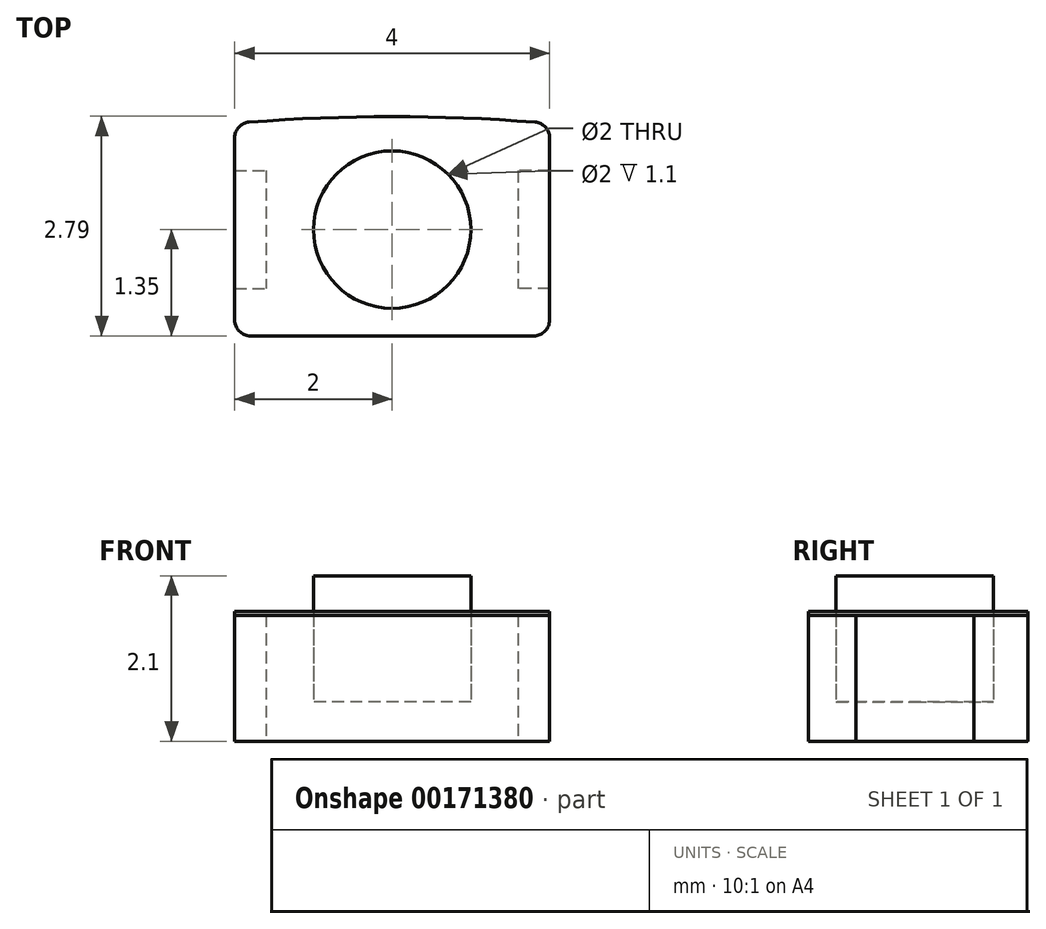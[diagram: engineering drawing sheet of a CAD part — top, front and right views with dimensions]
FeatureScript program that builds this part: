
annotation { "Feature Type Name" : "Feature", "Feature Type Description" : "" }
export const myFeature = defineFeature(function(context is Context, id is Id, definition is map)
    precondition{}
    {
        {
            var Q0;
            Q0=qCreatedBy(makeId("Top.planeOp"),FACE);
            var sketch = newSketch(context, id + "F0", { "sketchPlane" : qUnion([Q0])});
            skLineSegment(sketch, "E0.bottom", {"start": v(-2, 1.35) * mm, "end": v(2, 1.35) * mm});
            skLineSegment(sketch, "E0.top", {"start": v(-2, -1.35) * mm, "end": v(2, -1.35) * mm});
            skLineSegment(sketch, "E0.left", {"start": v(-2, 1.35) * mm, "end": v(-2, -1.35) * mm});
            skLineSegment(sketch, "E0.right", {"start": v(2, 1.35) * mm, "end": v(2, -1.35) * mm});
            skPoint(sketch, "E0.middle", {"position": v(0, 0) * mm});
            skLineSegment(sketch, "E1", {"start": v(0, 1.42) * mm, "end": v(0, -1.42) * mm});
            skPoint(sketch, "E1.endSnap0", {"position": v(0, -1.35) * mm});
            skArc(sketch, "E2", {"start": v(2, 1.35) * mm, "mid": v(0, 1.44) * mm, "end": v(-2, 1.35) * mm});
            skArc(sketch, "E3.MirrorCS", {"start": v(2, -1.35) * mm, "mid": v(0, -1.44) * mm, "end": v(-2, -1.35) * mm});
            skCircle(sketch, "E4", {"center": v(0, 0) * mm, "radius": 1 * mm});
            skLineSegment(sketch, "E5.bottom", {"start": v(-2, 0.75) * mm, "end": v(-1.6, 0.75) * mm});
            skLineSegment(sketch, "E5.top", {"start": v(-2, -0.75) * mm, "end": v(-1.6, -0.75) * mm});
            skLineSegment(sketch, "E5.left", {"start": v(-2, 0.75) * mm, "end": v(-2, -0.75) * mm});
            skLineSegment(sketch, "E5.right", {"start": v(-1.6, 0.75) * mm, "end": v(-1.6, -0.75) * mm});
            skPoint(sketch, "E6", {"position": v(-1.6, 0) * mm});
            skLineSegment(sketch, "E7.MirrorCS", {"start": v(2, -0.75) * mm, "end": v(1.6, -0.75) * mm});
            skLineSegment(sketch, "E8.MirrorCS", {"start": v(2, 0.75) * mm, "end": v(2, -0.75) * mm});
            skLineSegment(sketch, "E9.MirrorCS", {"start": v(2, 0.75) * mm, "end": v(1.6, 0.75) * mm});
            skLineSegment(sketch, "E10.MirrorCS", {"start": v(1.6, 0.75) * mm, "end": v(1.6, -0.75) * mm});
            skSolve(sketch);
        }
        {
            var Q0;
            {var subQ7=sQuery(id+"F0.wireOp",EDGE,"E5.bottom");Q0=makeQuery(id+"F0.imprint","IMPRINT",FACE,{"disambiguationData":[TD([[makeQuery(id+"F0.imprint","IMPRINT",EDGE,{"derivedFrom":subQ7}),1.0]])]});}
            var Q1;
            {var subQ0=sQuery(id+"F0.wireOp",EDGE,"E2");Q1=makeQuery(id+"F0.imprint","IMPRINT",FACE,{"disambiguationData":[TD([[makeQuery(id+"F0.imprint","IMPRINT",EDGE,{"derivedFrom":subQ0}),1.0]])]});}
            var Q2;
            {var subQ4=sQuery(id+"F0.wireOp",EDGE,"E7.MirrorCS");Q2=makeQuery(id+"F0.imprint","IMPRINT",FACE,{"disambiguationData":[TD([[makeQuery(id+"F0.imprint","IMPRINT",EDGE,{"derivedFrom":subQ4}),1.0]])]});}
            var Q3;
            {var subQ0=sQuery(id+"F0.wireOp",EDGE,"E3.MirrorCS");Q3=makeQuery(id+"F0.imprint","IMPRINT",FACE,{"disambiguationData":[TD([[makeQuery(id+"F0.imprint","IMPRINT",EDGE,{"derivedFrom":subQ0}),-1.0]])]});}
            extrude(context, id + "F1", {"entities" : qUnion([Q0, Q1, Q2, Q3]), "depth" : 1.6 * mm});
        }
        {
            var Q0;
            {var subQ0=sQuery(id+"F0.wireOp",EDGE,"E4");var subQ1=sQuery(id+"F0.wireOp",EDGE,"E1");var subQ2=makeQuery(id+"F0.imprint","INTERSECT",VERTEX,{"disambiguationData":[OD(0.0)],"derivedFrom":[subQ1,subQ0]});Q0=makeQuery(id+"F0.imprint","IMPRINT",FACE,{"disambiguationData":[TD([[makeQuery(id+"F0.imprint","IMPRINT",EDGE,{"disambiguationData":[TD([[subQ2,-1.0]])],"derivedFrom":subQ1}),-1.0]])]});}
            var Q1;
            {var subQ0=sQuery(id+"F0.wireOp",EDGE,"E4");var subQ1=sQuery(id+"F0.wireOp",EDGE,"E1");var subQ2=makeQuery(id+"F0.imprint","INTERSECT",VERTEX,{"disambiguationData":[OD(0.0)],"derivedFrom":[subQ1,subQ0]});Q1=makeQuery(id+"F0.imprint","IMPRINT",FACE,{"disambiguationData":[TD([[makeQuery(id+"F0.imprint","IMPRINT",EDGE,{"disambiguationData":[TD([[subQ2,-1.0]])],"derivedFrom":subQ1}),1.0]])]});}
            extrude(context, id + "F2", {"entities" : qUnion([Q0, Q1]), "operationType" : NewBodyOperationType.ADD, "depth" : 0.5 * mm});
        }
        {
            var Q0;
            Q0=makeQuery(id+"F0.imprint","IMPRINT",FACE,{"disambiguationData":[TD([[makeQuery(id+"F0.imprint","IMPRINT",EDGE,{"derivedFrom":sQuery(id+"F0.wireOp",EDGE,"E5.bottom")}),-1.0]])]});
            var Q1;
            Q1=makeQuery(id+"F0.imprint","IMPRINT",FACE,{"disambiguationData":[TD([[makeQuery(id+"F0.imprint","IMPRINT",EDGE,{"derivedFrom":sQuery(id+"F0.wireOp",EDGE,"E7.MirrorCS")}),-1.0]])]});
            extrude(context, id + "F3", {"entities" : qUnion([Q0, Q1]), "depth" : 1.6 * mm});
        }
        {
            var Q0;
            Q0=makeQuery(id+"F2.opExtrude","CAP_FACE",FACE,{"disambiguationData":[OSD([sQuery(id+"F0.wireOp",EDGE,"E4")])],"isStart":false});
            var sketch = newSketch(context, id + "F4", { "sketchPlane" : qUnion([Q0])});
            skCircle(sketch, "E11.0", {"center": v(0, 0) * mm, "radius": 1 * mm});
            skSolve(sketch);
        }
        {
            var Q0;
            Q0=makeQuery(id+"F4.imprint","IMPRINT",FACE,{"disambiguationData":[TD([[makeQuery(id+"F4.imprint","IMPRINT",EDGE,{"derivedFrom":sQuery(id+"F4.wireOp",EDGE,"E11.0")}),1.0]])]});
            extrude(context, id + "F5", {"entities" : qUnion([Q0]), "depth" : 1.6 * mm});
        }
        {
            var Q0;
            Q0=makeQuery(id+"F1.opExtrude","SWEPT_EDGE",EDGE,{"disambiguationData":[OSD([sQuery(id+"F0.wireOp",EDGE,"E0.top"),sQuery(id+"F0.wireOp",EDGE,"E0.left"),sQuery(id+"F0.wireOp",EDGE,"E3.MirrorCS")])]});
            var Q1;
            Q1=makeQuery(id+"F1.opExtrude","SWEPT_EDGE",EDGE,{"disambiguationData":[OSD([sQuery(id+"F0.wireOp",EDGE,"E0.top"),sQuery(id+"F0.wireOp",EDGE,"E0.right"),sQuery(id+"F0.wireOp",EDGE,"E3.MirrorCS")])]});
            var Q2;
            Q2=makeQuery(id+"F1.opExtrude","SWEPT_EDGE",EDGE,{"disambiguationData":[OSD([sQuery(id+"F0.wireOp",EDGE,"E0.bottom"),sQuery(id+"F0.wireOp",EDGE,"E0.left"),sQuery(id+"F0.wireOp",EDGE,"E2")])]});
            var Q3;
            Q3=makeQuery(id+"F1.opExtrude","SWEPT_EDGE",EDGE,{"disambiguationData":[OSD([sQuery(id+"F0.wireOp",EDGE,"E0.bottom"),sQuery(id+"F0.wireOp",EDGE,"E0.right"),sQuery(id+"F0.wireOp",EDGE,"E2")])]});
            fillet(context, id + "F6", {"entities" : qUnion([Q0, Q1, Q2, Q3]), "radius" : 0.2 * mm, "tangentPropagation" : true, "allowEdgeOverflow" : false});
        }
        {
            var Q0;
            Q0=makeQuery(id+"F1.opExtrude","CAP_FACE",FACE,{"disambiguationData":[OSD([sQuery(id+"F0.wireOp",EDGE,"E0.left"),sQuery(id+"F0.wireOp",EDGE,"E0.right"),sQuery(id+"F0.wireOp",EDGE,"E2"),sQuery(id+"F0.wireOp",EDGE,"E3.MirrorCS"),sQuery(id+"F0.wireOp",EDGE,"E4"),sQuery(id+"F0.wireOp",EDGE,"E5.bottom"),sQuery(id+"F0.wireOp",EDGE,"E5.top"),sQuery(id+"F0.wireOp",EDGE,"E5.right"),sQuery(id+"F0.wireOp",EDGE,"E7.MirrorCS"),sQuery(id+"F0.wireOp",EDGE,"E9.MirrorCS"),sQuery(id+"F0.wireOp",EDGE,"E10.MirrorCS")])],"isStart":false});
            var sketch = newSketch(context, id + "F7", { "sketchPlane" : qUnion([Q0])});
            skArc(sketch, "E12.0", {"start": v(1.82, 1.37) * mm, "mid": v(0, 1.44) * mm, "end": v(-1.82, 1.37) * mm});
            skLineSegment(sketch, "E12.1", {"start": v(-2, -0.75) * mm, "end": v(-2, -1.17) * mm});
            skArc(sketch, "E12.2", {"start": v(-2, -1.17) * mm, "mid": v(-1.95, -1.3) * mm, "end": v(-1.82, -1.37) * mm});
            skArc(sketch, "E12.3", {"start": v(-1.82, 1.37) * mm, "mid": v(-1.95, 1.3) * mm, "end": v(-2, 1.17) * mm});
            skLineSegment(sketch, "E12.4", {"start": v(-2, 1.17) * mm, "end": v(-2, 0.75) * mm});
            skArc(sketch, "E12.5", {"start": v(1.82, -1.37) * mm, "mid": v(0, -1.44) * mm, "end": v(-1.82, -1.37) * mm});
            skLineSegment(sketch, "E12.6", {"start": v(2, 1.17) * mm, "end": v(2, 0.75) * mm});
            skArc(sketch, "E12.7", {"start": v(2, 1.17) * mm, "mid": v(1.95, 1.3) * mm, "end": v(1.82, 1.37) * mm});
            skLineSegment(sketch, "E12.8", {"start": v(2, 0.75) * mm, "end": v(1.6, 0.75) * mm});
            skLineSegment(sketch, "E12.9", {"start": v(-2, 0.75) * mm, "end": v(-2, -0.75) * mm});
            skLineSegment(sketch, "E12.10", {"start": v(2, 0.75) * mm, "end": v(2, -0.75) * mm});
            skLineSegment(sketch, "E12.11", {"start": v(2, -0.75) * mm, "end": v(2, -1.17) * mm});
            skArc(sketch, "E12.12", {"start": v(1.82, -1.37) * mm, "mid": v(1.95, -1.3) * mm, "end": v(2, -1.17) * mm});
            skCircle(sketch, "E12.13", {"center": v(0, 0) * mm, "radius": 1 * mm});
            skSolve(sketch);
        }
        {
            var Q0;
            Q0=makeQuery(id+"F7.imprint","IMPRINT",FACE,{"disambiguationData":[TD([[makeQuery(id+"F7.imprint","IMPRINT",EDGE,{"derivedFrom":sQuery(id+"F7.wireOp",EDGE,"E12.0")}),1.0]])]});
            var Q1;
            Q1=makeQuery(id+"F7.imprint","IMPRINT",FACE,{"disambiguationData":[TD([[makeQuery(id+"F7.imprint","IMPRINT",EDGE,{"derivedFrom":sQuery(id+"F7.wireOp",EDGE,"E12.8")}),1.0]])]});
            var Q2;
            Q2=makeQuery(id+"F7.imprint","IMPRINT",FACE,{"disambiguationData":[TD([[makeQuery(id+"F7.imprint","IMPRINT",EDGE,{"derivedFrom":sQuery(id+"F7.wireOp",EDGE,"E12.9")}),1.0]])]});
            extrude(context, id + "F8", {"entities" : qUnion([Q0, Q1, Q2]), "depth" : 0.05 * mm});
        }
    });
